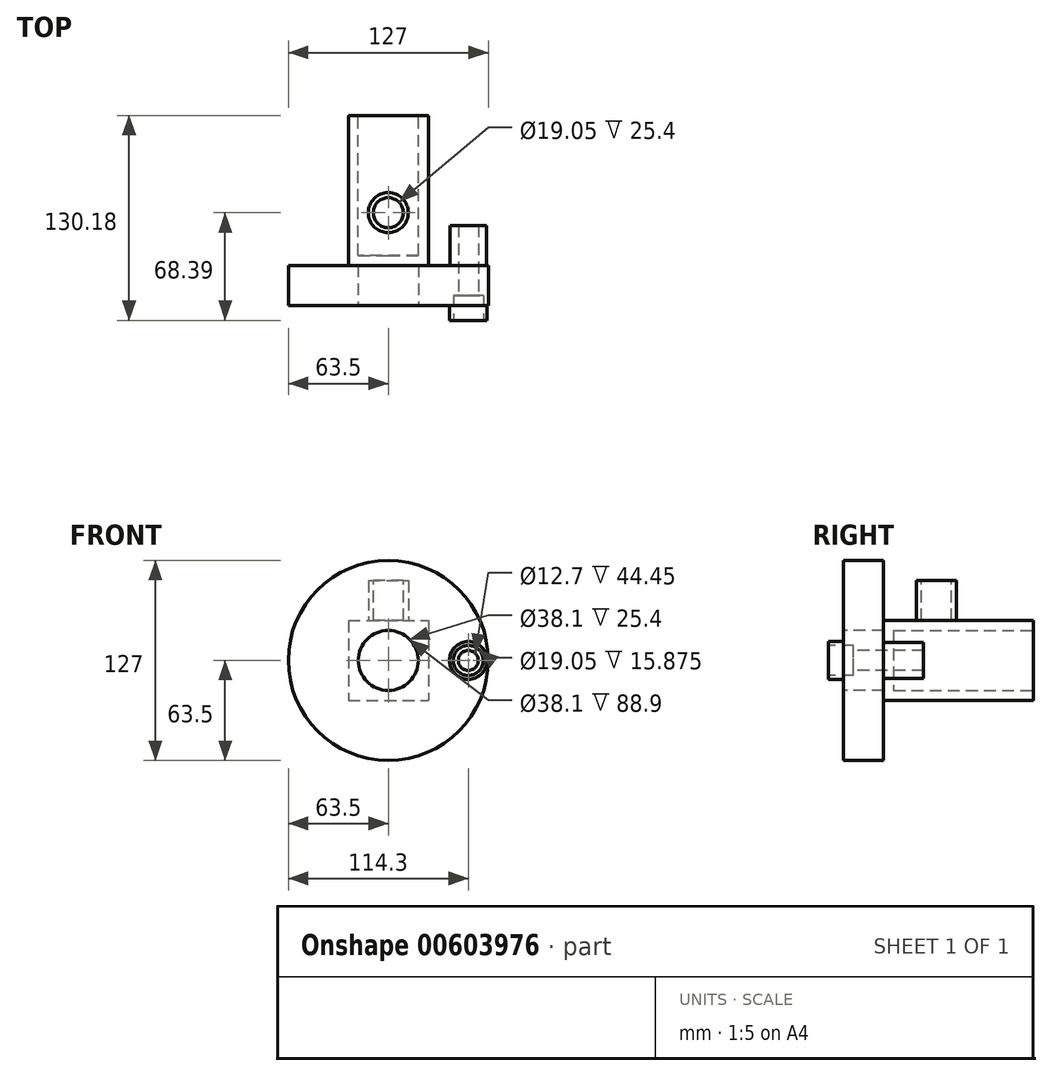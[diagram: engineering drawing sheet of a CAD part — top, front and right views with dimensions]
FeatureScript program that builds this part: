
annotation { "Feature Type Name" : "Feature", "Feature Type Description" : "" }
export const myFeature = defineFeature(function(context is Context, id is Id, definition is map)
    precondition{}
    {
        {
            var Q0;
            Q0=qCreatedBy(makeId("Front.planeOp"),FACE);
            var sketch = newSketch(context, id + "F0", { "sketchPlane" : qUnion([Q0])});
            skCircle(sketch, "E0", {"center": v(0, 0) * mm, "radius": 63.5 * mm});
            skSolve(sketch);
        }
        {
            var Q0;
            Q0 = qSketchRegion(id + "F0", true);
            extrude(context, id + "F1", {"entities" : qUnion([Q0]), "depth" : 25.4 * mm, "offsetDistance" : 25.4 * mm});
        }
        {
            var Q0;
            Q0=makeQuery(id+"F1.opExtrude","CAP_FACE",FACE,{"disambiguationData":[OSD([sQuery(id+"F0.wireOp",EDGE,"E0")])],"isStart":false});
            var sketch = newSketch(context, id + "F2", { "sketchPlane" : qUnion([Q0])});
            skCircle(sketch, "E1", {"center": v(0, 0) * mm, "radius": 19.05 * mm});
            skSolve(sketch);
        }
        {
            var Q0;
            Q0 = qSketchRegion(id + "F2", true);
            extrude(context, id + "F3", {"entities" : qUnion([Q0]), "operationType" : NewBodyOperationType.REMOVE, "endBound" : BoundingType.THROUGH_ALL, "oppositeDirection" : true, "depth" : 25.4 * mm, "offsetDistance" : 25.4 * mm});
        }
        {
            var Q0;
            Q0=makeQuery(id+"F1.opExtrude","CAP_FACE",FACE,{"disambiguationData":[OSD([sQuery(id+"F0.wireOp",EDGE,"E0")])],"isStart":false});
            var sketch = newSketch(context, id + "F4", { "sketchPlane" : qUnion([Q0])});
            skCircle(sketch, "E2", {"center": v(50.8, 0) * mm, "radius": 6.35 * mm});
            skSolve(sketch);
        }
        {
            var Q0;
            Q0=makeQuery(id+"F4.imprint","IMPRINT",FACE,{"disambiguationData":[TD([[makeQuery(id+"F4.imprint","IMPRINT",EDGE,{"derivedFrom":sQuery(id+"F4.wireOp",EDGE,"E2")}),1.0]])]});
            extrude(context, id + "F5", {"entities" : qUnion([Q0]), "operationType" : NewBodyOperationType.REMOVE, "oppositeDirection" : true, "depth" : 25.4 * mm, "offsetDistance" : 25.4 * mm});
        }
        {
            var Q0;
            Q0=makeQuery(id+"F1.opExtrude","CAP_FACE",FACE,{"disambiguationData":[OSD([sQuery(id+"F0.wireOp",EDGE,"E0")])],"isStart":false});
            var sketch = newSketch(context, id + "F6", { "sketchPlane" : qUnion([Q0])});
            skCircle(sketch, "E3", {"center": v(50.8, 0) * mm, "radius": 9.53 * mm});
            skSolve(sketch);
        }
        {
            var Q0;
            Q0 = qSketchRegion(id + "F6", true);
            extrude(context, id + "F7", {"entities" : qUnion([Q0]), "operationType" : NewBodyOperationType.REMOVE, "oppositeDirection" : true, "depth" : 6.35 * mm, "offsetDistance" : 25.4 * mm});
        }
        {
            var Q0;
            Q0=makeQuery(id+"F1.opExtrude","CAP_FACE",FACE,{"disambiguationData":[OSD([sQuery(id+"F0.wireOp",EDGE,"E0")])],"isStart":true});
            var sketch = newSketch(context, id + "F8", { "sketchPlane" : qUnion([Q0])});
            skLineSegment(sketch, "E4.bottom", {"start": v(25.4, 25.4) * mm, "end": v(-25.4, 25.4) * mm});
            skLineSegment(sketch, "E4.top", {"start": v(25.4, -25.4) * mm, "end": v(-25.4, -25.4) * mm});
            skLineSegment(sketch, "E4.left", {"start": v(25.4, 25.4) * mm, "end": v(25.4, -25.4) * mm});
            skLineSegment(sketch, "E4.right", {"start": v(-25.4, 25.4) * mm, "end": v(-25.4, -25.4) * mm});
            skPoint(sketch, "E4.middle", {"position": v(0, 0) * mm});
            skSolve(sketch);
        }
        {
            var Q0;
            Q0 = qSketchRegion(id + "F8", true);
            extrude(context, id + "F9", {"entities" : qUnion([Q0]), "operationType" : NewBodyOperationType.ADD, "depth" : 95.25 * mm, "offsetDistance" : 25.4 * mm});
        }
        {
            var Q0;
            Q0=makeQuery(id+"F9.opExtrude","CAP_FACE",FACE,{"disambiguationData":[OSD([sQuery(id+"F8.wireOp",EDGE,"E4.bottom"),sQuery(id+"F8.wireOp",EDGE,"E4.top"),sQuery(id+"F8.wireOp",EDGE,"E4.left"),sQuery(id+"F8.wireOp",EDGE,"E4.right")])],"isStart":false});
            var sketch = newSketch(context, id + "F10", { "sketchPlane" : qUnion([Q0])});
            skCircle(sketch, "E5", {"center": v(0, 0) * mm, "radius": 19.05 * mm});
            skSolve(sketch);
        }
        {
            var Q0;
            Q0 = qSketchRegion(id + "F10", true);
            extrude(context, id + "F11", {"entities" : qUnion([Q0]), "operationType" : NewBodyOperationType.REMOVE, "oppositeDirection" : true, "depth" : 88.9 * mm, "offsetDistance" : 25.4 * mm});
        }
        {
            var Q0;
            Q0=makeQuery(id+"F1.opExtrude","CAP_FACE",FACE,{"disambiguationData":[OSD([sQuery(id+"F0.wireOp",EDGE,"E0")])],"isStart":true});
            var sketch = newSketch(context, id + "F12", { "sketchPlane" : qUnion([Q0])});
            skCircle(sketch, "E6", {"center": v(-50.8, 0) * mm, "radius": 8.68 * mm});
            skCircle(sketch, "E7", {"center": v(-50.8, 0) * mm, "radius": 11.44 * mm});
            skSolve(sketch);
        }
        {
            var Q0;
            Q0=makeQuery(id+"F12.imprint","IMPRINT",FACE,{"disambiguationData":[TD([[makeQuery(id+"F12.imprint","IMPRINT",EDGE,{"derivedFrom":sQuery(id+"F12.wireOp",EDGE,"E6")}),-1.0]])]});
            var Q1;
            Q1=makeQuery(id+"F12.imprint","IMPRINT",FACE,{"disambiguationData":[TD([[makeQuery(id+"F12.imprint","IMPRINT",EDGE,{"derivedFrom":sQuery(id+"F12.wireOp",EDGE,"E6")}),1.0]])]});
            extrude(context, id + "F13", {"entities" : qUnion([Q0, Q1]), "operationType" : NewBodyOperationType.ADD, "depth" : 25.4 * mm, "offsetDistance" : 25.4 * mm});
        }
        {
            var Q0;
            Q0=makeQuery(id+"F9.opExtrude","SWEPT_FACE",FACE,{"disambiguationData":[OSD([sQuery(id+"F8.wireOp",EDGE,"E4.bottom")])]});
            var sketch = newSketch(context, id + "F14", { "sketchPlane" : qUnion([Q0])});
            skCircle(sketch, "E8", {"center": v(0, 33.46) * mm, "radius": 12.7 * mm});
            skSolve(sketch);
        }
        {
            var Q0;
            Q0 = qSketchRegion(id + "F14", true);
            extrude(context, id + "F15", {"entities" : qUnion([Q0]), "operationType" : NewBodyOperationType.ADD, "depth" : 25.4 * mm, "offsetDistance" : 25.4 * mm});
        }
        {
            var Q0;
            Q0=makeQuery(id+"F15.opExtrude","CAP_FACE",FACE,{"disambiguationData":[OSD([sQuery(id+"F14.wireOp",EDGE,"E8")])],"isStart":false});
            var sketch = newSketch(context, id + "F16", { "sketchPlane" : qUnion([Q0])});
            skCircle(sketch, "E9", {"center": v(0, 33.46) * mm, "radius": 9.53 * mm});
            skSolve(sketch);
        }
        {
            var Q0;
            Q0=makeQuery(id+"F16.imprint","IMPRINT",FACE,{"disambiguationData":[TD([[makeQuery(id+"F16.imprint","IMPRINT",EDGE,{"derivedFrom":sQuery(id+"F16.wireOp",EDGE,"E9")}),1.0]])]});
            extrude(context, id + "F17", {"entities" : qUnion([Q0]), "operationType" : NewBodyOperationType.REMOVE, "oppositeDirection" : true, "depth" : 25.4 * mm, "offsetDistance" : 25.4 * mm});
        }
        {
            var Q0;
            Q0=makeQuery(id+"F1.opExtrude","CAP_FACE",FACE,{"disambiguationData":[OSD([sQuery(id+"F0.wireOp",EDGE,"E0")])],"isStart":false});
            var sketch = newSketch(context, id + "F18", { "sketchPlane" : qUnion([Q0])});
            skCircle(sketch, "E10", {"center": v(50.8, 0) * mm, "radius": 11.99 * mm});
            skSolve(sketch);
        }
        {
            var Q0;
            Q0=makeQuery(id+"F18.imprint","IMPRINT",FACE,{"disambiguationData":[TD([[makeQuery(id+"F18.imprint","IMPRINT",EDGE,{"derivedFrom":sQuery(id+"F18.wireOp",EDGE,"E10")}),1.0]])]});
            extrude(context, id + "F19", {"entities" : qUnion([Q0]), "operationType" : NewBodyOperationType.ADD, "depth" : 9.52 * mm, "offsetDistance" : 25.4 * mm});
        }
    });
